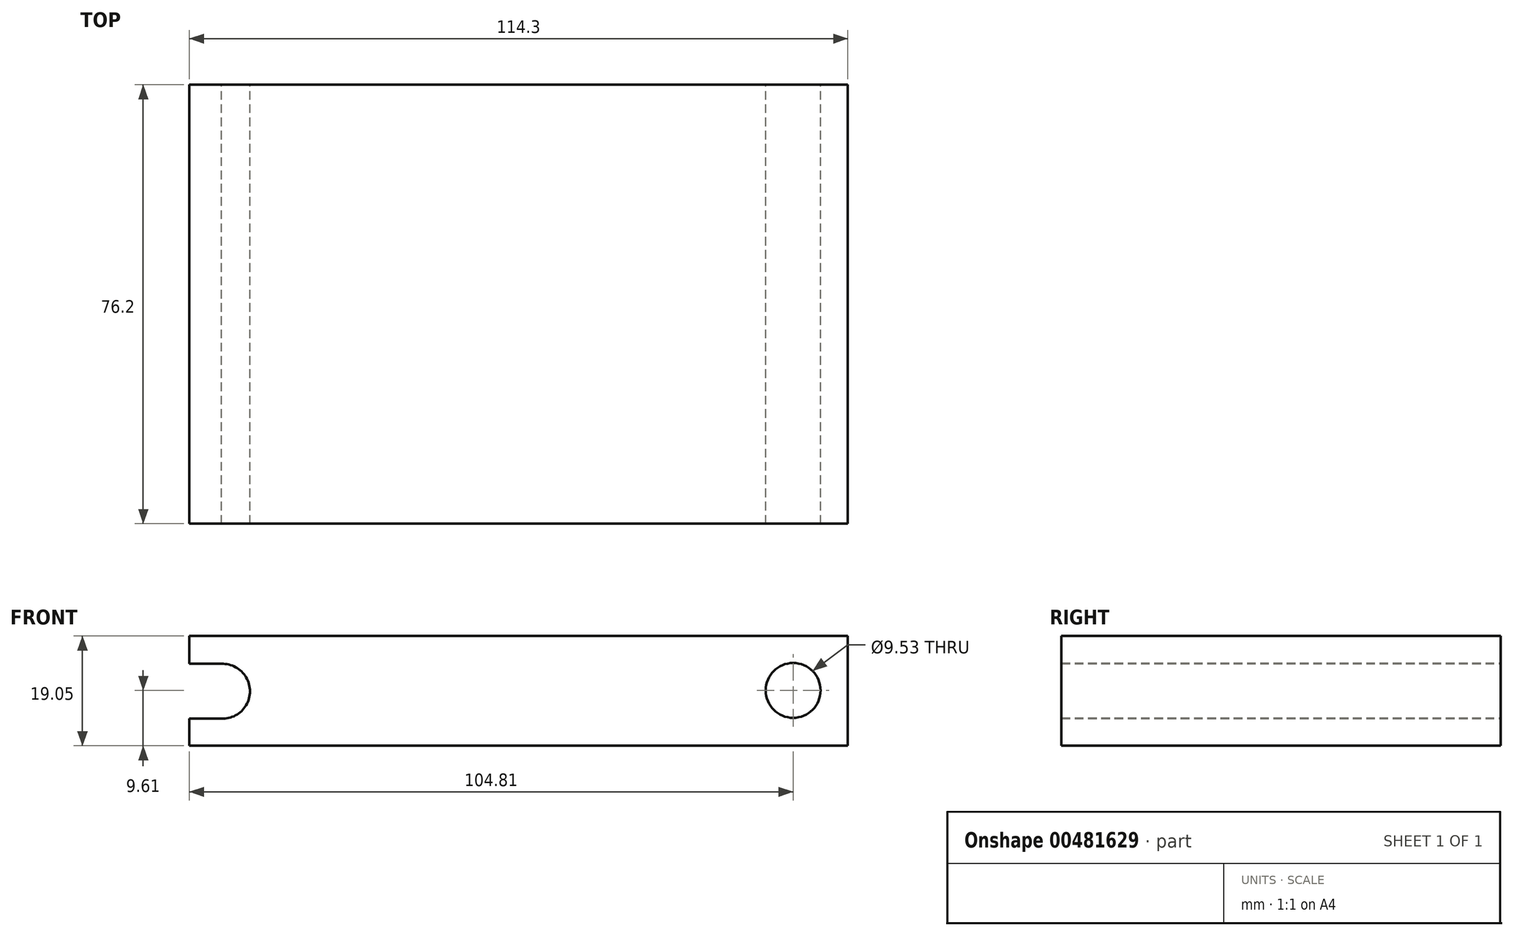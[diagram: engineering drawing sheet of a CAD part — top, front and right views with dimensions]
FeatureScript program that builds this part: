
annotation { "Feature Type Name" : "Feature", "Feature Type Description" : "" }
export const myFeature = defineFeature(function(context is Context, id is Id, definition is map)
    precondition{}
    {
        {
            var Q0;
            Q0=qCreatedBy(makeId("Front.planeOp"),FACE);
            var sketch = newSketch(context, id + "F0", { "sketchPlane" : qUnion([Q0])});
            skLineSegment(sketch, "E0.bottom", {"start": v(0, 0) * mm, "end": v(-114.3, 0) * mm});
            skLineSegment(sketch, "E0.top", {"start": v(0, 19.05) * mm, "end": v(-114.3, 19.05) * mm});
            skLineSegment(sketch, "E0.left", {"start": v(0, 0) * mm, "end": v(0, 19.05) * mm});
            skLineSegment(sketch, "E0.right", {"start": v(-114.3, 0) * mm, "end": v(-114.3, 19.05) * mm});
            skPoint(sketch, "E1.first.point", {"position": v(0, 9.53) * mm});
            skPoint(sketch, "E1.second.point", {"position": v(-18.97, 9.53) * mm});
            skPoint(sketch, "E1.second.point.positionSnap0", {"position": v(0, 9.53) * mm});
            skPoint(sketch, "E1.third.point", {"position": v(-8.58, 19.05) * mm});
            skCircle(sketch, "E2", {"center": v(-9.49, 9.6) * mm, "radius": 4.76 * mm});
            skCircle(sketch, "E3", {"center": v(-108.55, 9.46) * mm, "radius": 4.76 * mm});
            skLineSegment(sketch, "E4", {"start": v(-108.35, 4.7) * mm, "end": v(-114.3, 4.7) * mm});
            skLineSegment(sketch, "E5", {"start": v(-108.72, 14.22) * mm, "end": v(-114.3, 14.22) * mm});
            skSolve(sketch);
        }
        {
            var Q0;
            {var subQ1=sQuery(id+"F0.wireOp",EDGE,"E0.bottom");Q0=makeQuery(id+"F0.imprint","IMPRINT",FACE,{"disambiguationData":[TD([[makeQuery(id+"F0.imprint","IMPRINT",EDGE,{"derivedFrom":subQ1}),-1.0]])]});}
            extrude(context, id + "F1", {"entities" : qUnion([Q0]), "depth" : 76.2 * mm});
        }
        {
            var Q0;
            Q0=qCreatedBy(makeId("Top.planeOp"),FACE);
            var sketch = newSketch(context, id + "F2", { "sketchPlane" : qUnion([Q0])});
            skPoint(sketch, "E6.first.point", {"position": v(0, 0) * mm});
            skPoint(sketch, "E6.second.point", {"position": v(0, -25.4) * mm});
            skPoint(sketch, "E6.third.point", {"position": v(-12.06, -16.6) * mm});
            skCircle(sketch, "E7", {"center": v(-12.7, -25.4) * mm, "radius": 3.18 * mm});
            skCircle(sketch, "E8", {"center": v(-12.7, -50.88) * mm, "radius": 3.18 * mm});
            skSolve(sketch);
        }
        {
            var Q0;
            Q0=makeQuery(id+"F2.imprint","IMPRINT",FACE,{"disambiguationData":[TD([[makeQuery(id+"F2.imprint","IMPRINT",EDGE,{"derivedFrom":sQuery(id+"F2.wireOp",EDGE,"E8")}),1.0]])]});
            var Q1;
            Q1=makeQuery(id+"F2.imprint","IMPRINT",FACE,{"disambiguationData":[TD([[makeQuery(id+"F2.imprint","IMPRINT",EDGE,{"derivedFrom":sQuery(id+"F2.wireOp",EDGE,"E7")}),1.0]])]});
            var Q2;
            Q2=sQuery(id+"F2.wireOp",EDGE,"E8");
            var Q3;
            Q3=sQuery(id+"F2.wireOp",EDGE,"E7");
            var Q4;
            Q4=makeQuery(id+"F1.opExtrude","SWEPT_FACE",FACE,{"disambiguationData":[OSD([sQuery(id+"F0.wireOp",EDGE,"E0.bottom")])]});
            extrude(context, id + "F3", {"entities" : qUnion([Q0, Q1]), "bodyType" : ToolBodyType.SURFACE, "surfaceEntities" : qUnion([Q2, Q3]), "endBound" : BoundingType.SYMMETRIC, "endBoundEntityFace" : qUnion([Q4]), "depth" : 50.8 * mm, "hasSecondDirection" : true, "secondDirectionOppositeDirection" : true, "secondDirectionDepth" : 25.4 * mm});
        }
    });
